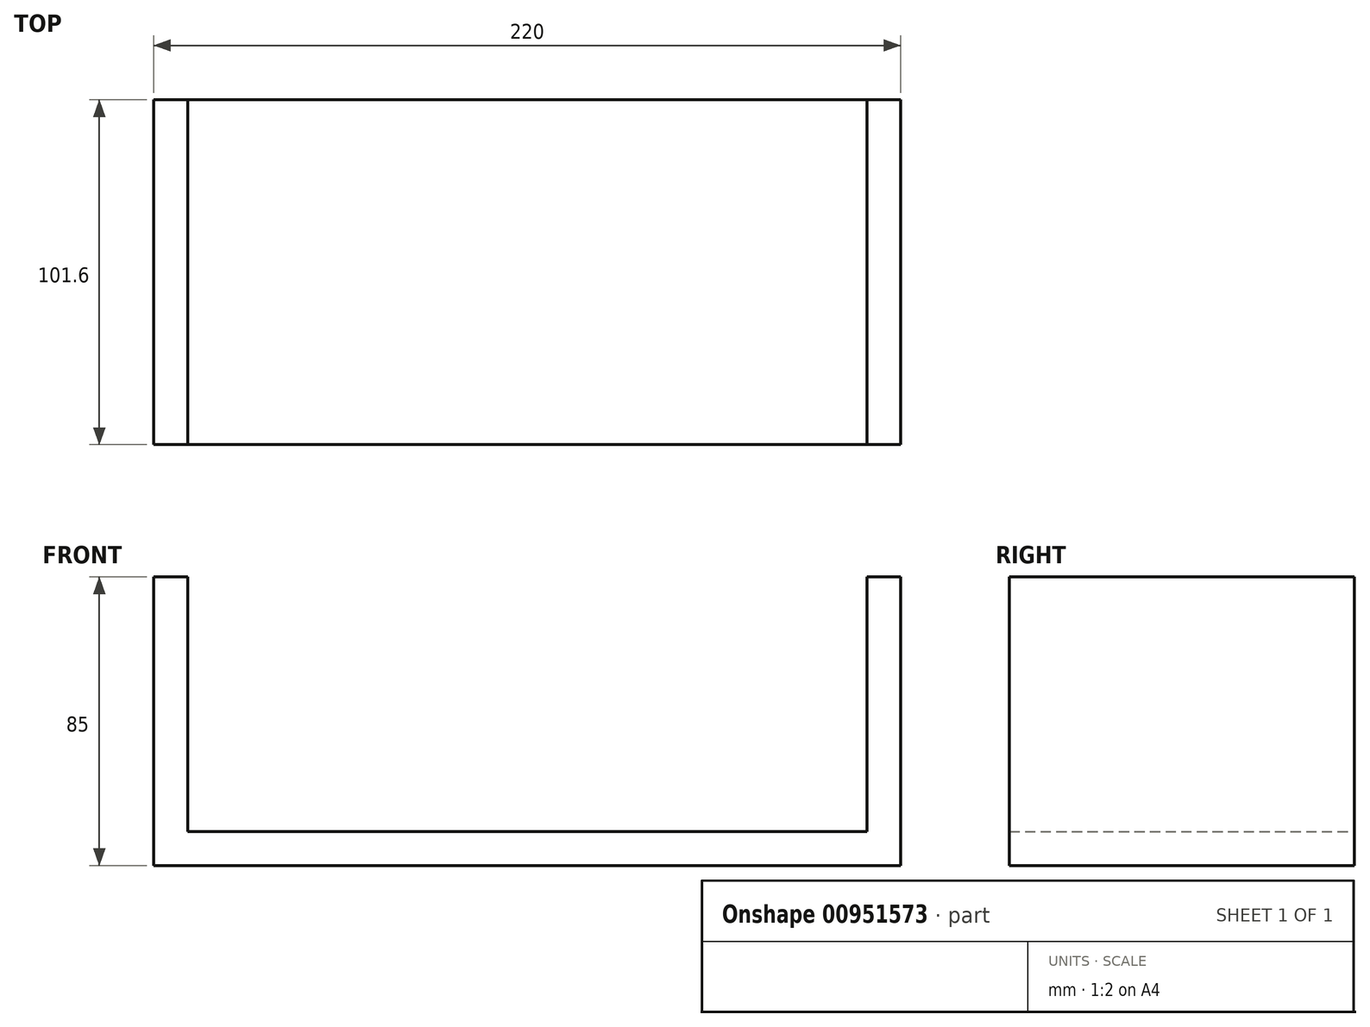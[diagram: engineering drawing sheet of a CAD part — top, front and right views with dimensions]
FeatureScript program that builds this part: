
annotation { "Feature Type Name" : "Feature", "Feature Type Description" : "" }
export const myFeature = defineFeature(function(context is Context, id is Id, definition is map)
    precondition{}
    {
        {
            var Q0;
            Q0=qCreatedBy(makeId("Front.planeOp"),FACE);
            var sketch = newSketch(context, id + "F0", { "sketchPlane" : qUnion([Q0])});
            skLineSegment(sketch, "E0", {"start": v(-100, 0) * mm, "end": v(-100, 75) * mm});
            skLineSegment(sketch, "E1", {"start": v(-100, 75) * mm, "end": v(-110, 75) * mm});
            skLineSegment(sketch, "E2", {"start": v(-110, 75) * mm, "end": v(-110, -10) * mm});
            skLineSegment(sketch, "E3", {"start": v(-110, -10) * mm, "end": v(110, -10) * mm});
            skLineSegment(sketch, "E4", {"start": v(110, -10) * mm, "end": v(110, 75) * mm});
            skLineSegment(sketch, "E5", {"start": v(110, 75) * mm, "end": v(100, 75) * mm});
            skLineSegment(sketch, "E6", {"start": v(100, 75) * mm, "end": v(100, 0) * mm});
            skLineSegment(sketch, "E7", {"start": v(100, 0) * mm, "end": v(-100, 0) * mm});
            skSolve(sketch);
        }
        {
            var Q0;
            Q0=makeQuery(id+"F0.imprint","IMPRINT",FACE,{"disambiguationData":[TD([[makeQuery(id+"F0.imprint","IMPRINT",EDGE,{"derivedFrom":sQuery(id+"F0.wireOp",EDGE,"E0")}),1.0]])]});
            extrude(context, id + "F1", {"entities" : qUnion([Q0]), "endBound" : BoundingType.SYMMETRIC, "depth" : 101.6 * mm, "offsetDistance" : 25.4 * mm});
        }
    });
